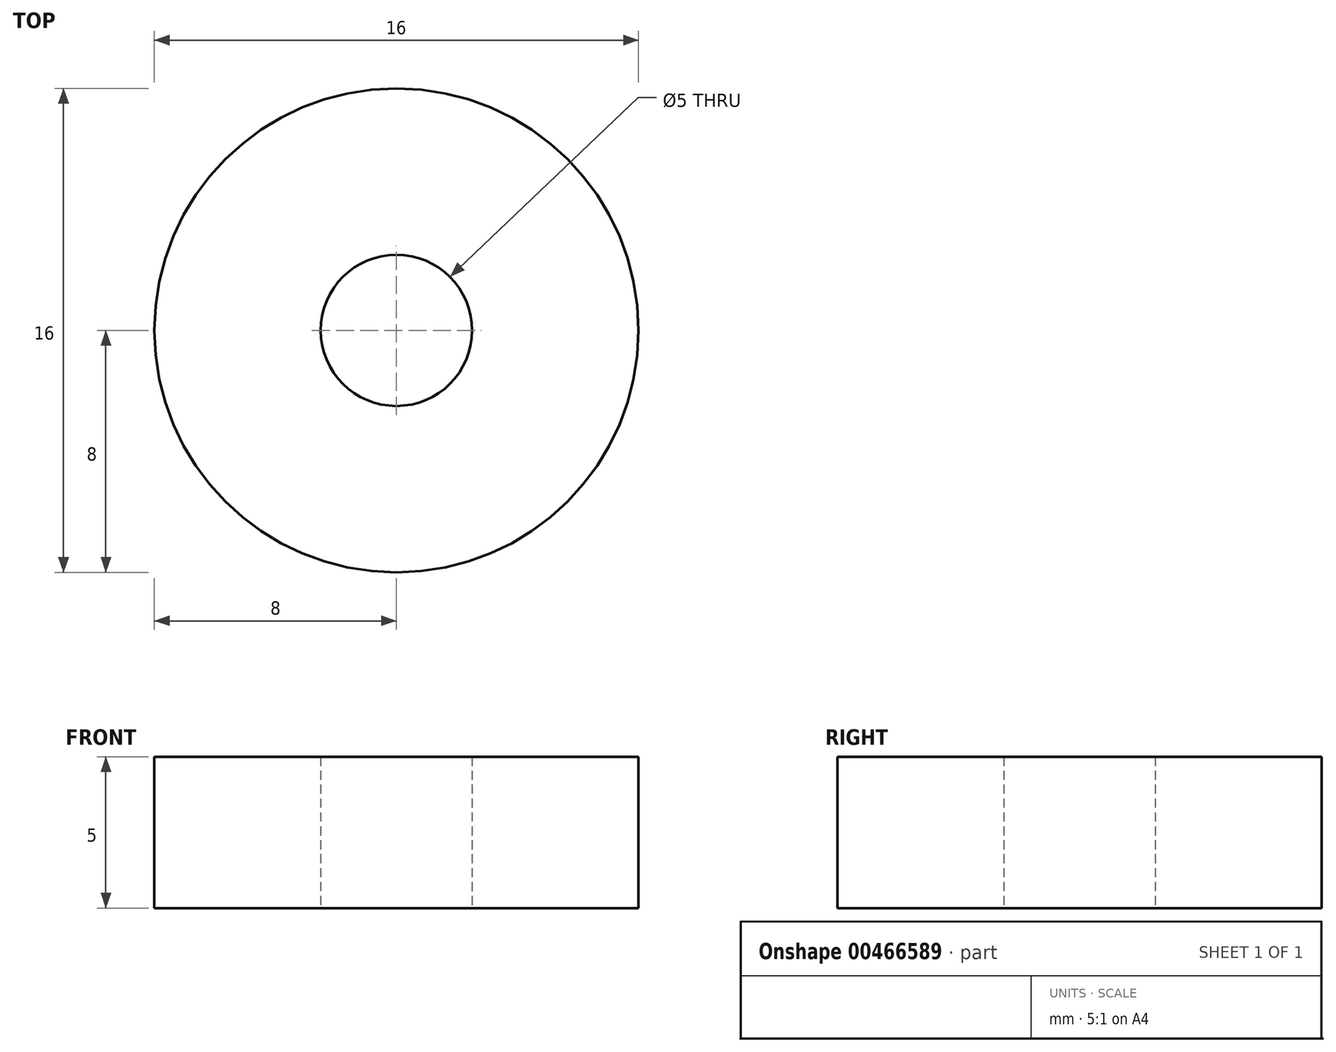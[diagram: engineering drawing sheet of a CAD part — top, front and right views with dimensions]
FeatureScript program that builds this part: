
annotation { "Feature Type Name" : "Feature", "Feature Type Description" : "" }
export const myFeature = defineFeature(function(context is Context, id is Id, definition is map)
    precondition{}
    {
        {
            var Q0;
            Q0=qCreatedBy(makeId("Top.planeOp"),FACE);
            var sketch = newSketch(context, id + "F0", { "sketchPlane" : qUnion([Q0])});
            skCircle(sketch, "E0", {"center": v(0, 0) * mm, "radius": 8 * mm});
            skCircle(sketch, "E1", {"center": v(0, 0) * mm, "radius": 2.5 * mm});
            skSolve(sketch);
        }
        {
            var Q0;
            Q0=qSketchRegion(id+"F0",true);
            extrude(context, id + "F1", {"entities" : qUnion([Q0]), "depth" : 5 * mm});
        }
    });
